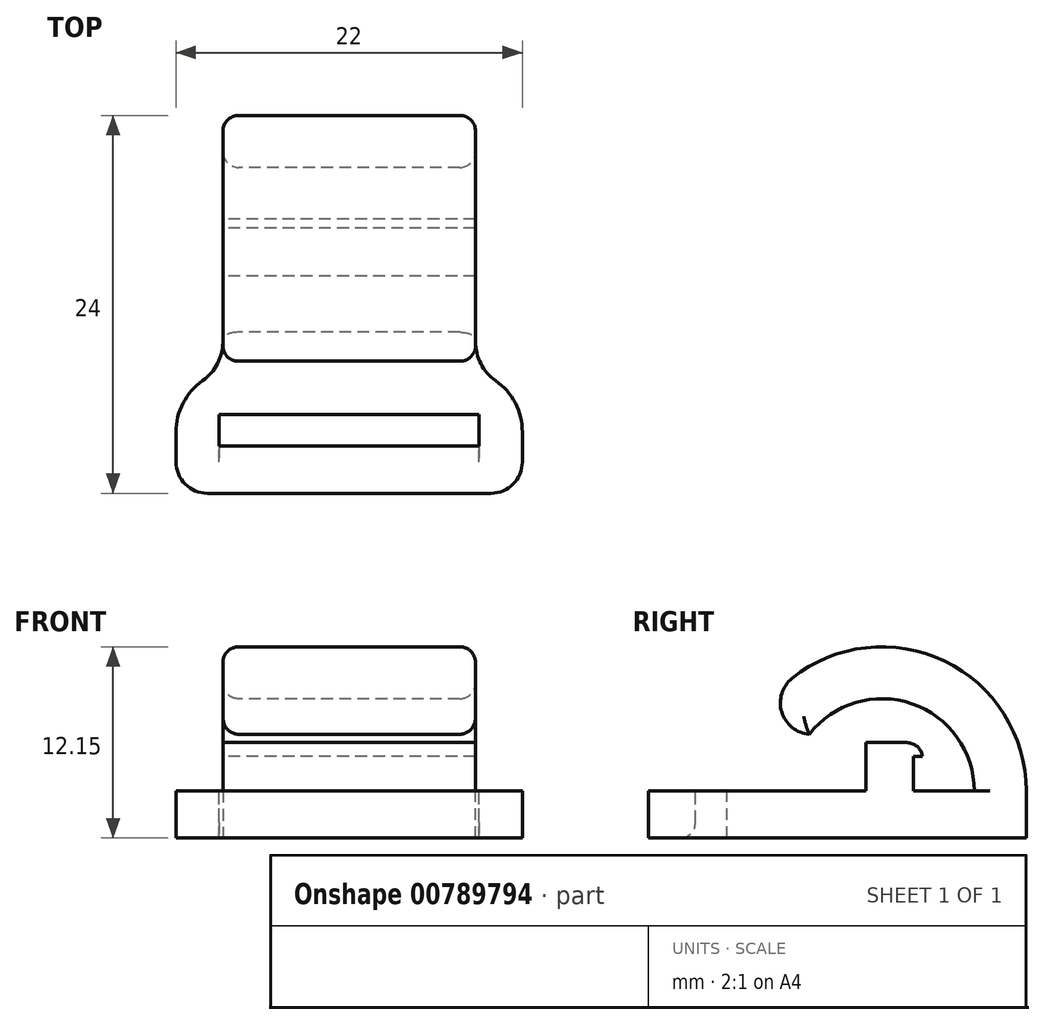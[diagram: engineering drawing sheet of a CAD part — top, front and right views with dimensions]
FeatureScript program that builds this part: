
annotation { "Feature Type Name" : "Feature", "Feature Type Description" : "" }
export const myFeature = defineFeature(function(context is Context, id is Id, definition is map)
    precondition{}
    {
        {
            var Q0;
            Q0=qCreatedBy(makeId("Top.planeOp"),FACE);
            var sketch = newSketch(context, id + "F0", { "sketchPlane" : qUnion([Q0])});
            skLineSegment(sketch, "E0.bottom", {"start": v(-8.03, 34.18) * mm, "end": v(8.02, 34.18) * mm});
            skLineSegment(sketch, "E0.top", {"start": v(-8.03, 30.88) * mm, "end": v(8.02, 30.88) * mm});
            skLineSegment(sketch, "E0.left", {"start": v(-8.03, 34.18) * mm, "end": v(-8.03, 30.88) * mm});
            skLineSegment(sketch, "E0.right", {"start": v(8.02, 34.18) * mm, "end": v(8.02, 30.88) * mm});
            skPoint(sketch, "E0.middle", {"position": v(0, 32.53) * mm});
            skLineSegment(sketch, "E1.bottom", {"start": v(-8.03, 19.18) * mm, "end": v(8.03, 19.18) * mm});
            skLineSegment(sketch, "E1.top", {"start": v(-8.03, 15.88) * mm, "end": v(8.03, 15.88) * mm});
            skLineSegment(sketch, "E1.left", {"start": v(-8.03, 19.18) * mm, "end": v(-8.03, 15.88) * mm});
            skLineSegment(sketch, "E1.right", {"start": v(8.03, 19.18) * mm, "end": v(8.03, 15.88) * mm});
            skPoint(sketch, "E1.middle", {"position": v(0, 17.53) * mm});
            skLineSegment(sketch, "E2", {"start": v(0, 32.53) * mm, "end": v(0, 17.53) * mm, "construction": true});
            skSolve(sketch);
        }
        {
            var Q0;
            Q0=sQuery(id+"F0.wireOp",EDGE,"E0.left");
            cPlane(context, id + "F1", {"entities" : qUnion([Q0]), "cplaneType" : CPlaneType.LINE_ANGLE, "offset" : 25 * mm, "angle" : 90 * degree, "width" : 150 * mm, "height" : 150 * mm});
        }
        {
            var Q0;
            Q0=qCreatedBy(id+"F1.planeOp",FACE);
            var sketch = newSketch(context, id + "F2", { "sketchPlane" : qUnion([Q0])});
            skArc(sketch, "E3", {"start": v(34.18, 0) * mm, "mid": v(25.03, 9.15) * mm, "end": v(15.88, 0) * mm});
            skLineSegment(sketch, "E4", {"start": v(34.18, 0) * mm, "end": v(15.88, 0) * mm, "construction": true});
            skArc(sketch, "E5", {"start": v(30.88, 0) * mm, "mid": v(25.03, 5.85) * mm, "end": v(19.18, 0) * mm});
            skLineSegment(sketch, "E6", {"start": v(34.18, 0) * mm, "end": v(30.88, 0) * mm});
            skLineSegment(sketch, "E7", {"start": v(19.18, 0) * mm, "end": v(15.88, 0) * mm});
            skSolve(sketch);
        }
        {
            var Q0;
            Q0=makeQuery(id+"F2.imprint","IMPRINT",FACE,{"disambiguationData":[TD([[makeQuery(id+"F2.imprint","IMPRINT",EDGE,{"derivedFrom":sQuery(id+"F2.wireOp",EDGE,"E3")}),1.0]])]});
            extrude(context, id + "F3", {"entities" : qUnion([Q0]), "depth" : 16.05 * mm, "offsetDistance" : 25 * mm});
        }
        {
            var Q0;
            Q0=qCreatedBy(makeId("Right.planeOp"),FACE);
            var sketch = newSketch(context, id + "F4", { "sketchPlane" : qUnion([Q0])});
            skLineSegment(sketch, "E8.bottom", {"start": v(20.62, 3.6) * mm, "end": v(15.2, 3.6) * mm});
            skLineSegment(sketch, "E8.top", {"start": v(20.62, 0) * mm, "end": v(15.2, 0) * mm});
            skLineSegment(sketch, "E8.left", {"start": v(20.62, 3.6) * mm, "end": v(20.62, 0) * mm});
            skLineSegment(sketch, "E8.right", {"start": v(15.2, 3.6) * mm, "end": v(15.2, 0) * mm});
            skSolve(sketch);
        }
        {
            var Q0;
            Q0 = qSketchRegion(id + "F4", true);
            extrude(context, id + "F5", {"entities" : qUnion([Q0]), "operationType" : NewBodyOperationType.REMOVE, "oppositeDirection" : true, "depth" : 25 * mm, "offsetDistance" : 25 * mm, "hasSecondDirection" : true, "secondDirectionOppositeDirection" : false, "secondDirectionDepth" : 25 * mm});
        }
        {
            var Q0;
            Q0=makeQuery(id+"F5.boolean.opBoolean","INTERSECT",EDGE,{"derivedFrom":[makeQuery(id+"F3.opExtrude","SWEPT_FACE",FACE,{"disambiguationData":[OSD([sQuery(id+"F2.wireOp",EDGE,"E3")])]}),makeQuery(id+"F5.opExtrude","SWEPT_FACE",FACE,{"disambiguationData":[OSD([sQuery(id+"F4.wireOp",EDGE,"E8.bottom")])]})]});
            fillet(context, id + "F6", {"entities" : qUnion([Q0]), "radius" : 2 * mm, "tangentPropagation" : true, "allowEdgeOverflow" : false});
        }
        {
            var Q0;
            Q0=qCreatedBy(makeId("Right.planeOp"),FACE);
            var sketch = newSketch(context, id + "F7", { "sketchPlane" : qUnion([Q0])});
            skLineSegment(sketch, "E9.bottom", {"start": v(27.01, 0) * mm, "end": v(23.99, 0) * mm});
            skLineSegment(sketch, "E9.left", {"start": v(27.01, 0) * mm, "end": v(27.01, 2.18) * mm});
            skLineSegment(sketch, "E9.right", {"start": v(23.99, 0) * mm, "end": v(23.99, 2.18) * mm});
            skLineSegment(sketch, "E10.bottom", {"start": v(27.01, 2.18) * mm, "end": v(27.59, 2.18) * mm});
            skLineSegment(sketch, "E10.top", {"start": v(23.99, 3.06) * mm, "end": v(27.59, 3.06) * mm});
            skLineSegment(sketch, "E10.right", {"start": v(27.59, 2.18) * mm, "end": v(27.59, 3.06) * mm});
            skLineSegment(sketch, "E11.bottom", {"start": v(34.18, 0) * mm, "end": v(10.18, 0) * mm});
            skLineSegment(sketch, "E11.top", {"start": v(34.18, -3) * mm, "end": v(10.18, -3) * mm});
            skLineSegment(sketch, "E11.left", {"start": v(34.18, 0) * mm, "end": v(34.18, -3) * mm});
            skLineSegment(sketch, "E11.right", {"start": v(10.18, 0) * mm, "end": v(10.18, -3) * mm});
            skLineSegment(sketch, "E12", {"start": v(23.99, 2.18) * mm, "end": v(23.99, 3.06) * mm});
            skSolve(sketch);
        }
        {
            var Q0;
            Q0 = qSketchRegion(id + "F7", true);
            extrude(context, id + "F8", {"entities" : qUnion([Q0]), "depth" : 8.03 * mm, "offsetDistance" : 25 * mm, "hasSecondDirection" : true, "secondDirectionOppositeDirection" : true, "secondDirectionDepth" : 8.03 * mm});
        }
        {
            var Q0;
            Q0=makeQuery(id+"F8.opExtrude","SWEPT_EDGE",EDGE,{"disambiguationData":[OSD([sQuery(id+"F7.wireOp",EDGE,"E10.top"),sQuery(id+"F7.wireOp",EDGE,"E10.right")])]});
            fillet(context, id + "F9", {"entities" : qUnion([Q0]), "radius" : 1 * mm, "tangentPropagation" : true, "allowEdgeOverflow" : false});
        }
        {
            var Q0;
            Q0=makeQuery(id+"F3.opExtrude","SWEPT_BODY",BODY,{"disambiguationData":[OSD([sQuery(id+"F2.wireOp",EDGE,"E3"),sQuery(id+"F2.wireOp",EDGE,"E5"),sQuery(id+"F2.wireOp",EDGE,"E6"),sQuery(id+"F2.wireOp",EDGE,"E7")])]});
            var Q1;
            Q1=makeQuery(id+"F8.opExtrude","SWEPT_BODY",BODY,{"disambiguationData":[OSD([sQuery(id+"F7.wireOp",EDGE,"E9.left"),sQuery(id+"F7.wireOp",EDGE,"E9.right"),sQuery(id+"F7.wireOp",EDGE,"E10.bottom"),sQuery(id+"F7.wireOp",EDGE,"E10.top"),sQuery(id+"F7.wireOp",EDGE,"E10.left"),sQuery(id+"F7.wireOp",EDGE,"E10.right"),sQuery(id+"F7.wireOp",EDGE,"E11.bottom"),sQuery(id+"F7.wireOp",EDGE,"E11.top"),sQuery(id+"F7.wireOp",EDGE,"E11.left"),sQuery(id+"F7.wireOp",EDGE,"E11.right")])]});
            booleanBodies(context, id + "F10", {"operationType" : BooleanOperationType.UNION, "tools" : qUnion([Q0, Q1])});
        }
        {
            var Q0;
            Q0=qCreatedBy(makeId("Right.planeOp"),FACE);
            var sketch = newSketch(context, id + "F11", { "sketchPlane" : qUnion([Q0])});
            skLineSegment(sketch, "E13.bottom", {"start": v(10.18, 0) * mm, "end": v(17.93, 0) * mm});
            skLineSegment(sketch, "E13.top", {"start": v(10.18, -3) * mm, "end": v(17.93, -3) * mm});
            skLineSegment(sketch, "E13.left", {"start": v(10.18, 0) * mm, "end": v(10.18, -3) * mm});
            skLineSegment(sketch, "E13.right", {"start": v(17.93, 0) * mm, "end": v(17.93, -3) * mm});
            skSolve(sketch);
        }
        {
            var Q0;
            Q0 = qSketchRegion(id + "F11", true);
            extrude(context, id + "F12", {"entities" : qUnion([Q0]), "operationType" : NewBodyOperationType.ADD, "depth" : 11 * mm, "offsetDistance" : 25 * mm, "hasSecondDirection" : true, "secondDirectionOppositeDirection" : true, "secondDirectionDepth" : 11 * mm});
        }
        {
            var Q0;
            Q0=qCreatedBy(makeId("Top.planeOp"),FACE);
            var sketch = newSketch(context, id + "F13", { "sketchPlane" : qUnion([Q0])});
            skLineSegment(sketch, "E14.bottom", {"start": v(-8.25, 15.18) * mm, "end": v(8.25, 15.18) * mm});
            skLineSegment(sketch, "E14.top", {"start": v(-8.25, 13.18) * mm, "end": v(8.25, 13.18) * mm});
            skLineSegment(sketch, "E14.left", {"start": v(-8.25, 15.18) * mm, "end": v(-8.25, 13.18) * mm});
            skLineSegment(sketch, "E14.right", {"start": v(8.25, 15.18) * mm, "end": v(8.25, 13.18) * mm});
            skPoint(sketch, "E14.middle", {"position": v(0, 14.18) * mm});
            skLineSegment(sketch, "E15", {"start": v(0, 13.18) * mm, "end": v(0, 34.18) * mm, "construction": true});
            skLineSegment(sketch, "E16", {"start": v(0, 13.18) * mm, "end": v(0, 10.18) * mm, "construction": true});
            skSolve(sketch);
        }
        {
            var Q0;
            Q0 = qSketchRegion(id + "F13", true);
            extrude(context, id + "F14", {"entities" : qUnion([Q0]), "operationType" : NewBodyOperationType.REMOVE, "oppositeDirection" : true, "depth" : 25 * mm, "offsetDistance" : 25 * mm});
        }
        {
            var Q0;
            Q0=makeQuery(id+"F14.boolean.opBoolean","INTERSECT",EDGE,{"derivedFrom":[makeQuery(id+"F12.boolean.opBoolean","MERGE",FACE,{"derivedFrom":[makeQuery(id+"F8.opExtrude","SWEPT_FACE",FACE,{"disambiguationData":[OSD([sQuery(id+"F7.wireOp",EDGE,"E11.top")])]}),makeQuery(id+"F12.opExtrude","SWEPT_FACE",FACE,{"disambiguationData":[OSD([sQuery(id+"F11.wireOp",EDGE,"E13.top")])]})]}),makeQuery(id+"F14.opExtrude","SWEPT_FACE",FACE,{"disambiguationData":[OSD([sQuery(id+"F13.wireOp",EDGE,"E14.top")])]})]});
            var Q1;
            Q1=makeQuery(id+"F14.boolean.opBoolean","COPY",EDGE,{"derivedFrom":makeQuery(id+"F14.opExtrude","CAP_EDGE",EDGE,{"disambiguationData":[OSD([sQuery(id+"F13.wireOp",EDGE,"E14.top")])],"isStart":true})});
            fillet(context, id + "F15", {"entities" : qUnion([Q0, Q1]), "radius" : 1 * mm, "tangentPropagation" : true, "allowEdgeOverflow" : false});
        }
        {
            var Q0;
            Q0=makeQuery(id+"F12.opExtrude","CAP_EDGE",EDGE,{"disambiguationData":[OSD([sQuery(id+"F11.wireOp",EDGE,"E13.right")])],"isStart":true});
            var Q1;
            Q1=makeQuery(id+"F12.opExtrude","CAP_EDGE",EDGE,{"disambiguationData":[OSD([sQuery(id+"F11.wireOp",EDGE,"E13.right")])],"isStart":false});
            fillet(context, id + "F16", {"entities" : qUnion([Q0, Q1]), "radius" : 4 * mm, "tangentPropagation" : true, "allowEdgeOverflow" : false});
        }
        {
            var Q0;
            Q0=makeQuery(id+"F3.opExtrude","CAP_EDGE",EDGE,{"disambiguationData":[OSD([sQuery(id+"F2.wireOp",EDGE,"E3")])],"isStart":true});
            var Q1;
            Q1=makeQuery(id+"F3.opExtrude","CAP_EDGE",EDGE,{"disambiguationData":[OSD([sQuery(id+"F2.wireOp",EDGE,"E3")])],"isStart":false});
            var Q2;
            Q2=makeQuery(id+"F3.opExtrude","CAP_EDGE",EDGE,{"disambiguationData":[OSD([sQuery(id+"F2.wireOp",EDGE,"E5")])],"isStart":true});
            var Q3;
            Q3=makeQuery(id+"F3.opExtrude","CAP_EDGE",EDGE,{"disambiguationData":[OSD([sQuery(id+"F2.wireOp",EDGE,"E5")])],"isStart":false});
            fillet(context, id + "F17", {"entities" : qUnion([Q0, Q1, Q2, Q3]), "radius" : 1 * mm, "tangentPropagation" : true, "allowEdgeOverflow" : false});
        }
        {
            var Q0;
            Q0=makeQuery(id+"F12.opExtrude","CAP_EDGE",EDGE,{"disambiguationData":[OSD([sQuery(id+"F11.wireOp",EDGE,"E13.left")])],"isStart":true});
            var Q1;
            Q1=makeQuery(id+"F12.opExtrude","CAP_EDGE",EDGE,{"disambiguationData":[OSD([sQuery(id+"F11.wireOp",EDGE,"E13.left")])],"isStart":false});
            fillet(context, id + "F18", {"entities" : qUnion([Q0, Q1]), "radius" : 2 * mm, "tangentPropagation" : true, "allowEdgeOverflow" : false});
        }
        {
            var Q0;
            Q0=makeQuery(id+"F16.opFillet","BLEND_EDGE",EDGE,{"blendedFrom":[makeQuery(id+"F12.opExtrude","CAP_EDGE",EDGE,{"disambiguationData":[OSD([sQuery(id+"F11.wireOp",EDGE,"E13.right")])],"isStart":true}),makeQuery(id+"F10.opBoolean","MERGE",FACE,{"derivedFrom":[makeQuery(id+"F3.opExtrude","CAP_FACE",FACE,{"disambiguationData":[OSD([sQuery(id+"F2.wireOp",EDGE,"E3"),sQuery(id+"F2.wireOp",EDGE,"E5"),sQuery(id+"F2.wireOp",EDGE,"E6"),sQuery(id+"F2.wireOp",EDGE,"E7")])],"isStart":true}),makeQuery(id+"F8.opExtrude","CAP_FACE",FACE,{"disambiguationData":[OSD([sQuery(id+"F7.wireOp",EDGE,"E9.left"),sQuery(id+"F7.wireOp",EDGE,"E9.right"),sQuery(id+"F7.wireOp",EDGE,"E10.bottom"),sQuery(id+"F7.wireOp",EDGE,"E10.top"),sQuery(id+"F7.wireOp",EDGE,"E10.right"),sQuery(id+"F7.wireOp",EDGE,"E11.bottom"),sQuery(id+"F7.wireOp",EDGE,"E11.top"),sQuery(id+"F7.wireOp",EDGE,"E11.left"),sQuery(id+"F7.wireOp",EDGE,"E11.right"),sQuery(id+"F7.wireOp",EDGE,"E12")])],"isStart":true})]})],"blendedInto":[makeQuery(id+"F10.opBoolean","MERGE",FACE,{"derivedFrom":[makeQuery(id+"F3.opExtrude","CAP_FACE",FACE,{"disambiguationData":[OSD([sQuery(id+"F2.wireOp",EDGE,"E3"),sQuery(id+"F2.wireOp",EDGE,"E5"),sQuery(id+"F2.wireOp",EDGE,"E6"),sQuery(id+"F2.wireOp",EDGE,"E7")])],"isStart":true}),makeQuery(id+"F8.opExtrude","CAP_FACE",FACE,{"disambiguationData":[OSD([sQuery(id+"F7.wireOp",EDGE,"E9.left"),sQuery(id+"F7.wireOp",EDGE,"E9.right"),sQuery(id+"F7.wireOp",EDGE,"E10.bottom"),sQuery(id+"F7.wireOp",EDGE,"E10.top"),sQuery(id+"F7.wireOp",EDGE,"E10.right"),sQuery(id+"F7.wireOp",EDGE,"E11.bottom"),sQuery(id+"F7.wireOp",EDGE,"E11.top"),sQuery(id+"F7.wireOp",EDGE,"E11.left"),sQuery(id+"F7.wireOp",EDGE,"E11.right"),sQuery(id+"F7.wireOp",EDGE,"E12")])],"isStart":true})]})]});
            var Q1;
            Q1=makeQuery(id+"F16.opFillet","BLEND_EDGE",EDGE,{"blendedFrom":[makeQuery(id+"F12.opExtrude","CAP_EDGE",EDGE,{"disambiguationData":[OSD([sQuery(id+"F11.wireOp",EDGE,"E13.right")])],"isStart":false}),makeQuery(id+"F10.opBoolean","MERGE",FACE,{"derivedFrom":[makeQuery(id+"F3.opExtrude","CAP_FACE",FACE,{"disambiguationData":[OSD([sQuery(id+"F2.wireOp",EDGE,"E3"),sQuery(id+"F2.wireOp",EDGE,"E5"),sQuery(id+"F2.wireOp",EDGE,"E6"),sQuery(id+"F2.wireOp",EDGE,"E7")])],"isStart":false}),makeQuery(id+"F8.opExtrude","CAP_FACE",FACE,{"disambiguationData":[OSD([sQuery(id+"F7.wireOp",EDGE,"E9.left"),sQuery(id+"F7.wireOp",EDGE,"E9.right"),sQuery(id+"F7.wireOp",EDGE,"E10.bottom"),sQuery(id+"F7.wireOp",EDGE,"E10.top"),sQuery(id+"F7.wireOp",EDGE,"E10.right"),sQuery(id+"F7.wireOp",EDGE,"E11.bottom"),sQuery(id+"F7.wireOp",EDGE,"E11.top"),sQuery(id+"F7.wireOp",EDGE,"E11.left"),sQuery(id+"F7.wireOp",EDGE,"E11.right"),sQuery(id+"F7.wireOp",EDGE,"E12")])],"isStart":false})]})],"blendedInto":[makeQuery(id+"F10.opBoolean","MERGE",FACE,{"derivedFrom":[makeQuery(id+"F3.opExtrude","CAP_FACE",FACE,{"disambiguationData":[OSD([sQuery(id+"F2.wireOp",EDGE,"E3"),sQuery(id+"F2.wireOp",EDGE,"E5"),sQuery(id+"F2.wireOp",EDGE,"E6"),sQuery(id+"F2.wireOp",EDGE,"E7")])],"isStart":false}),makeQuery(id+"F8.opExtrude","CAP_FACE",FACE,{"disambiguationData":[OSD([sQuery(id+"F7.wireOp",EDGE,"E9.left"),sQuery(id+"F7.wireOp",EDGE,"E9.right"),sQuery(id+"F7.wireOp",EDGE,"E10.bottom"),sQuery(id+"F7.wireOp",EDGE,"E10.top"),sQuery(id+"F7.wireOp",EDGE,"E10.right"),sQuery(id+"F7.wireOp",EDGE,"E11.bottom"),sQuery(id+"F7.wireOp",EDGE,"E11.top"),sQuery(id+"F7.wireOp",EDGE,"E11.left"),sQuery(id+"F7.wireOp",EDGE,"E11.right"),sQuery(id+"F7.wireOp",EDGE,"E12")])],"isStart":false})]})]});
            fillet(context, id + "F19", {"entities" : qUnion([Q0, Q1]), "radius" : 3 * mm, "tangentPropagation" : true, "allowEdgeOverflow" : false});
        }
    });
